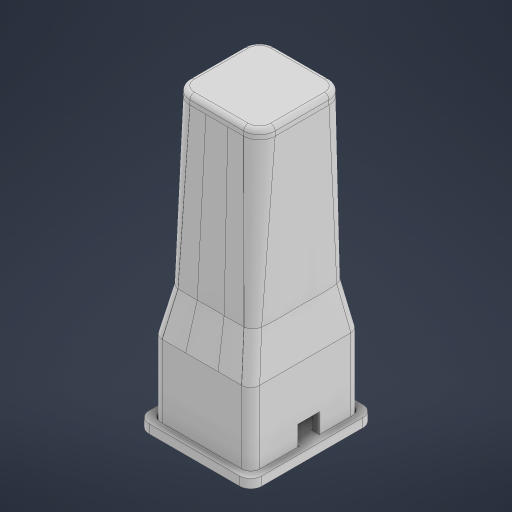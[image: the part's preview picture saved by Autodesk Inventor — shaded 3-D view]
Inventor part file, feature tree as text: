
AUTODESK INVENTOR PART (.ipt)
format: ipt  version: 2024.1 (Build 281209000, 209)  size: 1,970,688 bytes
history: native  units: mm
features: other x3, extrude x1, sketch x1, projected_geometry x1
ambient origin geometry x8: Origin, YZ Plane, XZ Plane, XY Plane, X Axis, Y Axis, Z Axis, Center Point
bodies: Body1 (feature_tree)
feature tree (6):
  other  "CloakTop.ipt"
  extrude  "Extrusion1"  Depth=10.0mm
  other  "Solid2::CloakTop.ipt"
  other  "TaggingFeature1"
  sketch  "Sketch2"  dims[d0=10.0mm d1=3.0mm d2=0.4mm d3=0.4mm d4=3.0mm d5=3.0mm d6=3.0mm d7=5.0mm d8=4.0mm d9=0.0mm]
  projected_geometry  "Project Cut Edges1"
